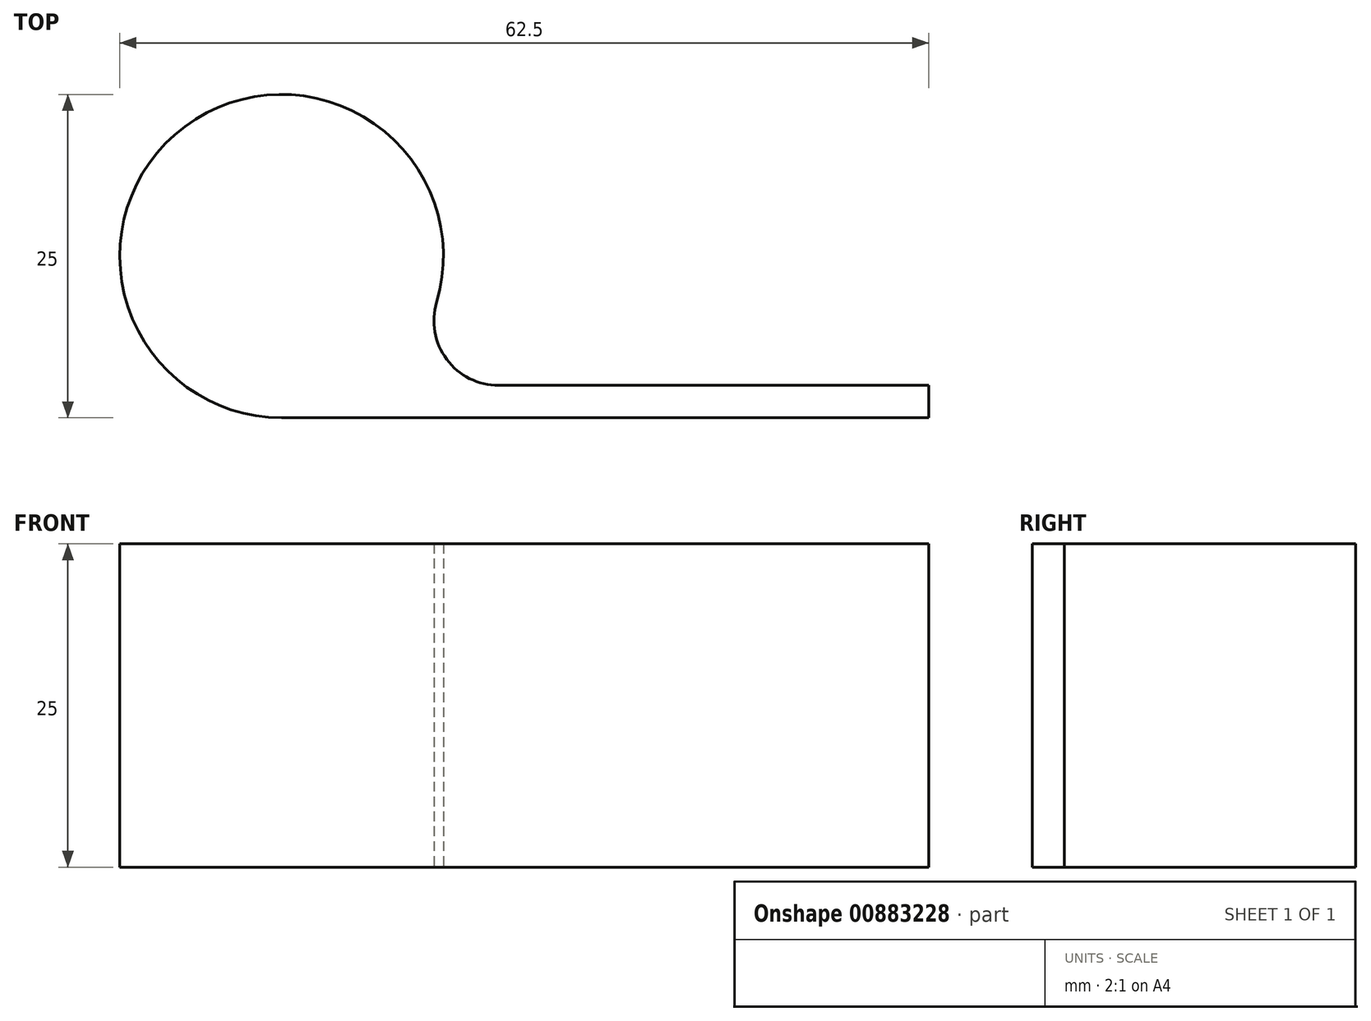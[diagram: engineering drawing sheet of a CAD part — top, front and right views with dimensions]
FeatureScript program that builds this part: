
annotation { "Feature Type Name" : "Feature", "Feature Type Description" : "" }
export const myFeature = defineFeature(function(context is Context, id is Id, definition is map)
    precondition{}
    {
        {
            var Q0;
            Q0=qCreatedBy(makeId("Top.planeOp"),FACE);
            var sketch = newSketch(context, id + "F0", { "sketchPlane" : qUnion([Q0])});
            skArc(sketch, "E0", {"start": v(11.98, -3.57) * mm, "mid": v(-7.47, 10.02) * mm, "end": v(0, -12.5) * mm});
            skLineSegment(sketch, "E1", {"start": v(0, -12.5) * mm, "end": v(50, -12.5) * mm});
            skLineSegment(sketch, "E2", {"start": v(50, -12.5) * mm, "end": v(50, -10) * mm});
            skLineSegment(sketch, "E3", {"start": v(50, -10) * mm, "end": v(16.77, -10) * mm});
            skPoint(sketch, "E4.visualSharp", {"position": v(7.5, -10) * mm});
            skArc(sketch, "E4.filletArc", {"start": v(11.98, -3.57) * mm, "mid": v(12.76, -7.99) * mm, "end": v(16.77, -10) * mm});
            skSolve(sketch);
        }
        {
            var Q0;
            Q0 = qSketchRegion(id + "F0", true);
            extrude(context, id + "F1", {"entities" : qUnion([Q0]), "depth" : 25 * mm, "offsetDistance" : 25 * mm});
        }
    });
